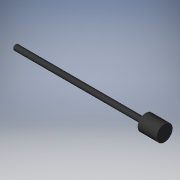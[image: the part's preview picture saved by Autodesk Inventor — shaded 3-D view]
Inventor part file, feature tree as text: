
AUTODESK INVENTOR PART (.ipt)
format: ipt  version: 2019 (Build 230136000, 136)  size: 145,408 bytes
history: native  units: mm
features: other x42, revolve x3, sketch x3
ambient origin geometry x8: Origin, YZ Plane, XZ Plane, XY Plane, X Axis, Y Axis, Z Axis, Center Point
bodies: Solid1 (feature_tree)
feature tree (48):
  revolve  "Revolution1"  Angle=360.0deg
  revolve  "Revolution2"  [1 undecoded]
  revolve  "Revolution3"  [1 undecoded]
  other  "a_XY"
  other  "a_YZ"
  other  "a_ZX"
  other  "a_X"
  other  "a_Y"
  other  "a_Z"
  other  "a_Center"
  other  "c1_XY"
  other  "c1_YZ"
  other  "c1_ZX"
  other  "c1_X"
  other  "c1_Y"
  other  "c1_Z"
  other  "c1_Center"
  other  "cc1_XY"
  other  "cc1_YZ"
  other  "cc1_ZX"
  other  "cc1_X"
  other  "cc1_Y"
  other  "cc1_Z"
  other  "cc1_Center"
  other  "cc2_XY"
  other  "cc2_YZ"
  other  "cc2_ZX"
  other  "cc2_X"
  other  "cc2_Y"
  other  "cc2_Z"
  other  "cc2_Center"
  other  "kk_XY"
  other  "kk_YZ"
  other  "kk_ZX"
  other  "kk_X"
  other  "kk_Y"
  other  "kk_Z"
  other  "kk_Center"
  other  "rod_XY"
  other  "rod_YZ"
  other  "rod_ZX"
  other  "rod_X"
  other  "rod_Y"
  other  "rod_Z"
  other  "rod_Center"
  sketch  "Sketch_1"  dims[d0=360.0deg d1=360.0deg]
  sketch  "Sketch_3"  dims[d2=360.0deg d3=0.0mm d4=0.0mm]
  sketch  "Sketch_4"
note: 2 required parameter values undecoded (feature->parameter linkage not recoverable at this tier; creation-order binding heuristic only, values carry confidence <= 0.55)